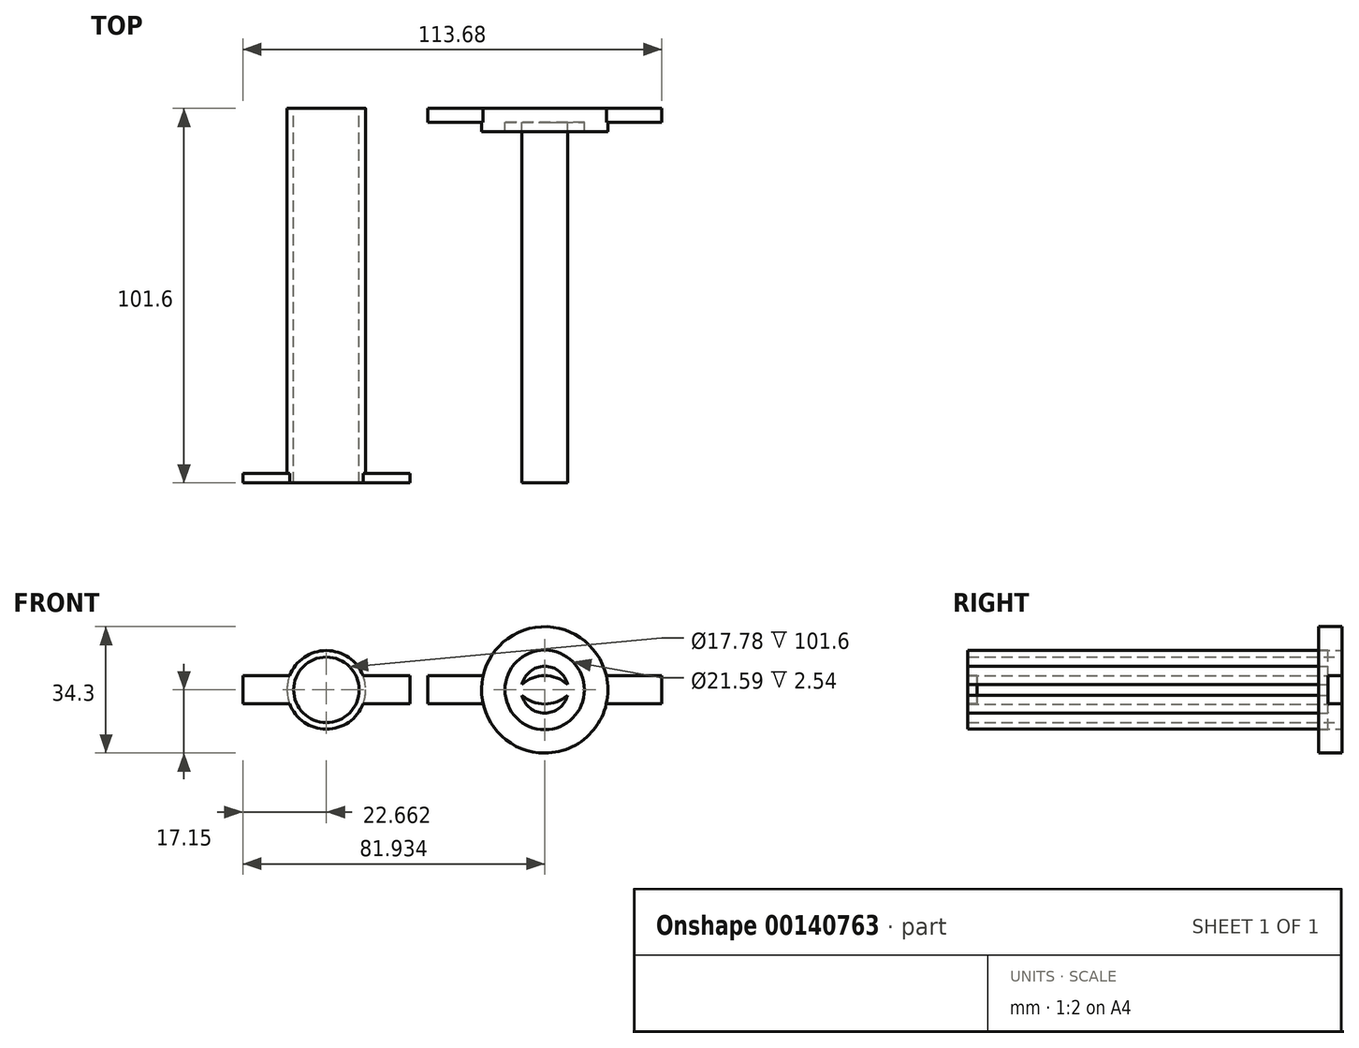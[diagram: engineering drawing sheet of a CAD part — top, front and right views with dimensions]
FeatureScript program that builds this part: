
annotation { "Feature Type Name" : "Feature", "Feature Type Description" : "" }
export const myFeature = defineFeature(function(context is Context, id is Id, definition is map)
    precondition{}
    {
        {
            var Q0;
            Q0=qCreatedBy(makeId("Front.planeOp"),FACE);
            var sketch = newSketch(context, id + "F0", { "sketchPlane" : qUnion([Q0])});
            skCircle(sketch, "E0", {"center": v(0, 0) * mm, "radius": 12.7 * mm});
            skCircle(sketch, "E1", {"center": v(0, 0) * mm, "radius": 15.24 * mm});
            skPoint(sketch, "E2.center", {"position": v(66.03, 0) * mm});
            skLineSegment(sketch, "E3", {"start": v(34.28, 0) * mm, "end": v(34.28, 3.8) * mm});
            skLineSegment(sketch, "E4", {"start": v(34.28, 3.8) * mm, "end": v(49.32, 3.8) * mm});
            skLineSegment(sketch, "E5", {"start": v(34.28, 0) * mm, "end": v(34.28, -3.81) * mm});
            skLineSegment(sketch, "E6", {"start": v(34.28, -3.81) * mm, "end": v(49.32, -3.81) * mm});
            skCircle(sketch, "E7", {"center": v(66.03, 0) * mm, "radius": 15.88 * mm});
            skCircle(sketch, "E8", {"center": v(66.03, 0) * mm, "radius": 17.15 * mm});
            skLineSegment(sketch, "E9.MirrorCS", {"start": v(97.78, -3.81) * mm, "end": v(82.75, -3.81) * mm});
            skLineSegment(sketch, "E10.MirrorCS", {"start": v(97.78, 0) * mm, "end": v(97.78, -3.81) * mm});
            skLineSegment(sketch, "E11.MirrorCS", {"start": v(97.78, 3.8) * mm, "end": v(82.75, 3.8) * mm});
            skLineSegment(sketch, "E12.MirrorCS", {"start": v(97.78, 0) * mm, "end": v(97.78, 3.8) * mm});
            skSolve(sketch);
        }
        {
            var Q0;
            Q0=makeQuery(id+"F0.imprint","IMPRINT",FACE,{"disambiguationData":[TD([[makeQuery(id+"F0.imprint","IMPRINT",EDGE,{"derivedFrom":sQuery(id+"F0.wireOp",EDGE,"WYK5WIV5-LSHk-n524-mOr9-z27NABO4Qitl")}),-1.0]])]});
            var Q1;
            Q1=makeQuery(id+"F0.imprint","IMPRINT",FACE,{"disambiguationData":[TD([[makeQuery(id+"F0.imprint","IMPRINT",EDGE,{"derivedFrom":sQuery(id+"F0.wireOp",EDGE,"E3")}),-1.0]])]});
            var Q2;
            {var subQ1=sQuery(id+"F0.wireOp",EDGE,"E9.MirrorCS");Q2=makeQuery(id+"F0.imprint","IMPRINT",FACE,{"disambiguationData":[TD([[makeQuery(id+"F0.imprint","IMPRINT",EDGE,{"derivedFrom":subQ1}),-1.0]])]});}
            var Q3;
            Q3=makeQuery(id+"F0.imprint","IMPRINT",FACE,{"disambiguationData":[TD([[makeQuery(id+"F0.imprint","IMPRINT",EDGE,{"derivedFrom":sQuery(id+"F0.wireOp",EDGE,"E7")}),-1.0]])]});
            var Q4;
            Q4=makeQuery(id+"F0.imprint","IMPRINT",FACE,{"disambiguationData":[TD([[makeQuery(id+"F0.imprint","IMPRINT",EDGE,{"derivedFrom":sQuery(id+"F0.wireOp",EDGE,"WYK5WIV5-LSHk-n524-mOr9-z27NABO4Qitl")}),1.0]])]});
            var Q5;
            Q5=makeQuery(id+"F0.imprint","IMPRINT",FACE,{"disambiguationData":[TD([[makeQuery(id+"F0.imprint","IMPRINT",EDGE,{"derivedFrom":sQuery(id+"F0.wireOp",EDGE,"E2.3.0")}),1.0]])]});
            var Q6;
            Q6=makeQuery(id+"F0.imprint","IMPRINT",FACE,{"disambiguationData":[TD([[makeQuery(id+"F0.imprint","IMPRINT",EDGE,{"derivedFrom":sQuery(id+"F0.wireOp",EDGE,"E2.2.0")}),1.0]])]});
            var Q7;
            Q7=makeQuery(id+"F0.imprint","IMPRINT",FACE,{"disambiguationData":[TD([[makeQuery(id+"F0.imprint","IMPRINT",EDGE,{"derivedFrom":sQuery(id+"F0.wireOp",EDGE,"E2.1.0")}),1.0]])]});
            var Q8;
            Q8=makeQuery(id+"F0.imprint","IMPRINT",FACE,{"disambiguationData":[TD([[makeQuery(id+"F0.imprint","IMPRINT",EDGE,{"derivedFrom":sQuery(id+"F0.wireOp",EDGE,"E7")}),1.0]])]});
            extrude(context, id + "F1", {"entities" : qUnion([Q0, Q1, Q2, Q3, Q4, Q5, Q6, Q7, Q8]), "depth" : 3.8 * mm});
        }
        {
            var Q0;
            Q0=makeQuery(id+"F1.opExtrude","CAP_FACE",FACE,{"disambiguationData":[OSD([sQuery(id+"F0.wireOp",EDGE,"WYK5WIV5-LSHk-n524-mOr9-z27NABO4Qitl"),sQuery(id+"F0.wireOp",EDGE,"E2.1.0"),sQuery(id+"F0.wireOp",EDGE,"E2.2.0"),sQuery(id+"F0.wireOp",EDGE,"E2.3.0"),sQuery(id+"F0.wireOp",EDGE,"E3"),sQuery(id+"F0.wireOp",EDGE,"E4"),sQuery(id+"F0.wireOp",EDGE,"E5"),sQuery(id+"F0.wireOp",EDGE,"E6"),sQuery(id+"F0.wireOp",EDGE,"E8"),sQuery(id+"F0.wireOp",EDGE,"E9.MirrorCS"),sQuery(id+"F0.wireOp",EDGE,"E10.MirrorCS"),sQuery(id+"F0.wireOp",EDGE,"E11.MirrorCS"),sQuery(id+"F0.wireOp",EDGE,"E12.MirrorCS")])],"isStart":false});
            var sketch = newSketch(context, id + "F2", { "sketchPlane" : qUnion([Q0])});
            skLineSegment(sketch, "E13.0.0", {"start": v(34.28, 3.8) * mm, "end": v(34.28, -3.81) * mm});
            skLineSegment(sketch, "E13.0.1", {"start": v(34.28, -3.81) * mm, "end": v(49.32, -3.81) * mm});
            skArc(sketch, "E13.0.2", {"start": v(49.32, -3.81) * mm, "mid": v(66.03, -17.15) * mm, "end": v(82.75, -3.8) * mm});
            skLineSegment(sketch, "E13.0.3", {"start": v(82.75, -3.81) * mm, "end": v(97.78, -3.81) * mm});
            skLineSegment(sketch, "E13.0.4", {"start": v(97.78, -3.81) * mm, "end": v(97.78, 3.8) * mm});
            skLineSegment(sketch, "E13.0.5", {"start": v(97.78, 3.8) * mm, "end": v(82.75, 3.8) * mm});
            skArc(sketch, "E13.0.6", {"start": v(82.75, 3.8) * mm, "mid": v(66.03, 17.15) * mm, "end": v(49.32, 3.8) * mm});
            skLineSegment(sketch, "E13.0.7", {"start": v(49.32, 3.8) * mm, "end": v(34.28, 3.8) * mm});
            skCircle(sketch, "E14", {"center": v(66.03, 0) * mm, "radius": 10.8 * mm});
            skCircle(sketch, "E15", {"center": v(66.03, 0) * mm, "radius": 17.15 * mm});
            skSolve(sketch);
        }
        {
            var Q0;
            Q0=makeQuery(id+"F2.imprint","IMPRINT",FACE,{"disambiguationData":[TD([[makeQuery(id+"F2.imprint","IMPRINT",EDGE,{"derivedFrom":sQuery(id+"F2.wireOp",EDGE,"E14")}),-1.0]])]});
            extrude(context, id + "F3", {"entities" : qUnion([Q0]), "operationType" : NewBodyOperationType.ADD, "depth" : 2.54 * mm});
        }
        {
            var Q0;
            Q0=qCreatedBy(makeId("Front.planeOp"),FACE);
            var sketch = newSketch(context, id + "F4", { "sketchPlane" : qUnion([Q0])});
            skCircle(sketch, "E16", {"center": v(6.76, 0) * mm, "radius": 10.67 * mm});
            skCircle(sketch, "E17", {"center": v(6.76, 0) * mm, "radius": 8.9 * mm});
            skSolve(sketch);
        }
        {
            var Q0;
            Q0 = qSketchRegion(id + "F4", true);
            extrude(context, id + "F5", {"entities" : qUnion([Q0]), "depth" : 101.6 * mm});
        }
        {
            var Q0;
            Q0=qCreatedBy(makeId("Front.planeOp"),FACE);
            var sketch = newSketch(context, id + "F6", { "sketchPlane" : qUnion([Q0])});
            skArc(sketch, "E18", {"start": v(72.23, 1.43) * mm, "mid": v(66.03, 6.39) * mm, "end": v(59.84, 1.43) * mm});
            skLineSegment(sketch, "E19", {"start": v(66.03, 0.04) * mm, "end": v(66.03, 3.85) * mm});
            skArc(sketch, "E20", {"start": v(72.23, 1.43) * mm, "mid": v(66.03, 3.85) * mm, "end": v(59.84, 1.43) * mm});
            skArc(sketch, "E21.MirrorCS", {"start": v(72.23, -1.43) * mm, "mid": v(66.03, -3.85) * mm, "end": v(59.84, -1.43) * mm});
            skArc(sketch, "E22.trimOffspring", {"start": v(59.86, -1.46) * mm, "mid": v(66.03, -6.31) * mm, "end": v(72.2, -1.46) * mm});
            skSolve(sketch);
        }
        {
            var Q0;
            Q0 = qSketchRegion(id + "F6", true);
            extrude(context, id + "F7", {"entities" : qUnion([Q0]), "operationType" : NewBodyOperationType.ADD, "depth" : 101.6 * mm});
        }
        {
            var Q0;
            Q0=makeQuery(id+"F5.opExtrude","CAP_FACE",FACE,{"disambiguationData":[OSD([sQuery(id+"F4.wireOp",EDGE,"E16"),sQuery(id+"F4.wireOp",EDGE,"E17")])],"isStart":false});
            var sketch = newSketch(context, id + "F8", { "sketchPlane" : qUnion([Q0])});
            skCircle(sketch, "E23.0", {"center": v(6.76, 0) * mm, "radius": 8.9 * mm});
            skLineSegment(sketch, "E24", {"start": v(6.76, 0) * mm, "end": v(6.76, 3.81) * mm});
            skLineSegment(sketch, "E25", {"start": v(-3.2, 3.81) * mm, "end": v(-15.9, 3.81) * mm});
            skLineSegment(sketch, "E26", {"start": v(-15.9, 3.81) * mm, "end": v(-15.9, -3.81) * mm});
            skPoint(sketch, "E27.start.orphan", {"position": v(6.76, -3.81) * mm});
            skLineSegment(sketch, "E28", {"start": v(-15.9, -3.81) * mm, "end": v(-3.2, -3.81) * mm});
            skLineSegment(sketch, "E29.MirrorCS", {"start": v(29.43, -3.81) * mm, "end": v(16.73, -3.81) * mm});
            skLineSegment(sketch, "E30.MirrorCS", {"start": v(29.43, 3.81) * mm, "end": v(29.43, -3.81) * mm});
            skLineSegment(sketch, "E31.MirrorCS", {"start": v(16.73, 3.81) * mm, "end": v(29.43, 3.81) * mm});
            skSolve(sketch);
        }
        {
            var Q0;
            {var subQ0=sQuery(id+"F8.wireOp",EDGE,"E25");Q0=makeQuery(id+"F8.imprint","IMPRINT",FACE,{"disambiguationData":[TD([[makeQuery(id+"F8.imprint","IMPRINT",EDGE,{"derivedFrom":subQ0}),1.0]])]});}
            var Q1;
            {var subQ0=sQuery(id+"F8.wireOp",EDGE,"E29.MirrorCS");Q1=makeQuery(id+"F8.imprint","IMPRINT",FACE,{"disambiguationData":[TD([[makeQuery(id+"F8.imprint","IMPRINT",EDGE,{"derivedFrom":subQ0}),-1.0]])]});}
            extrude(context, id + "F9", {"entities" : qUnion([Q0, Q1]), "operationType" : NewBodyOperationType.ADD, "oppositeDirection" : true, "depth" : 2.54 * mm});
        }
    });
